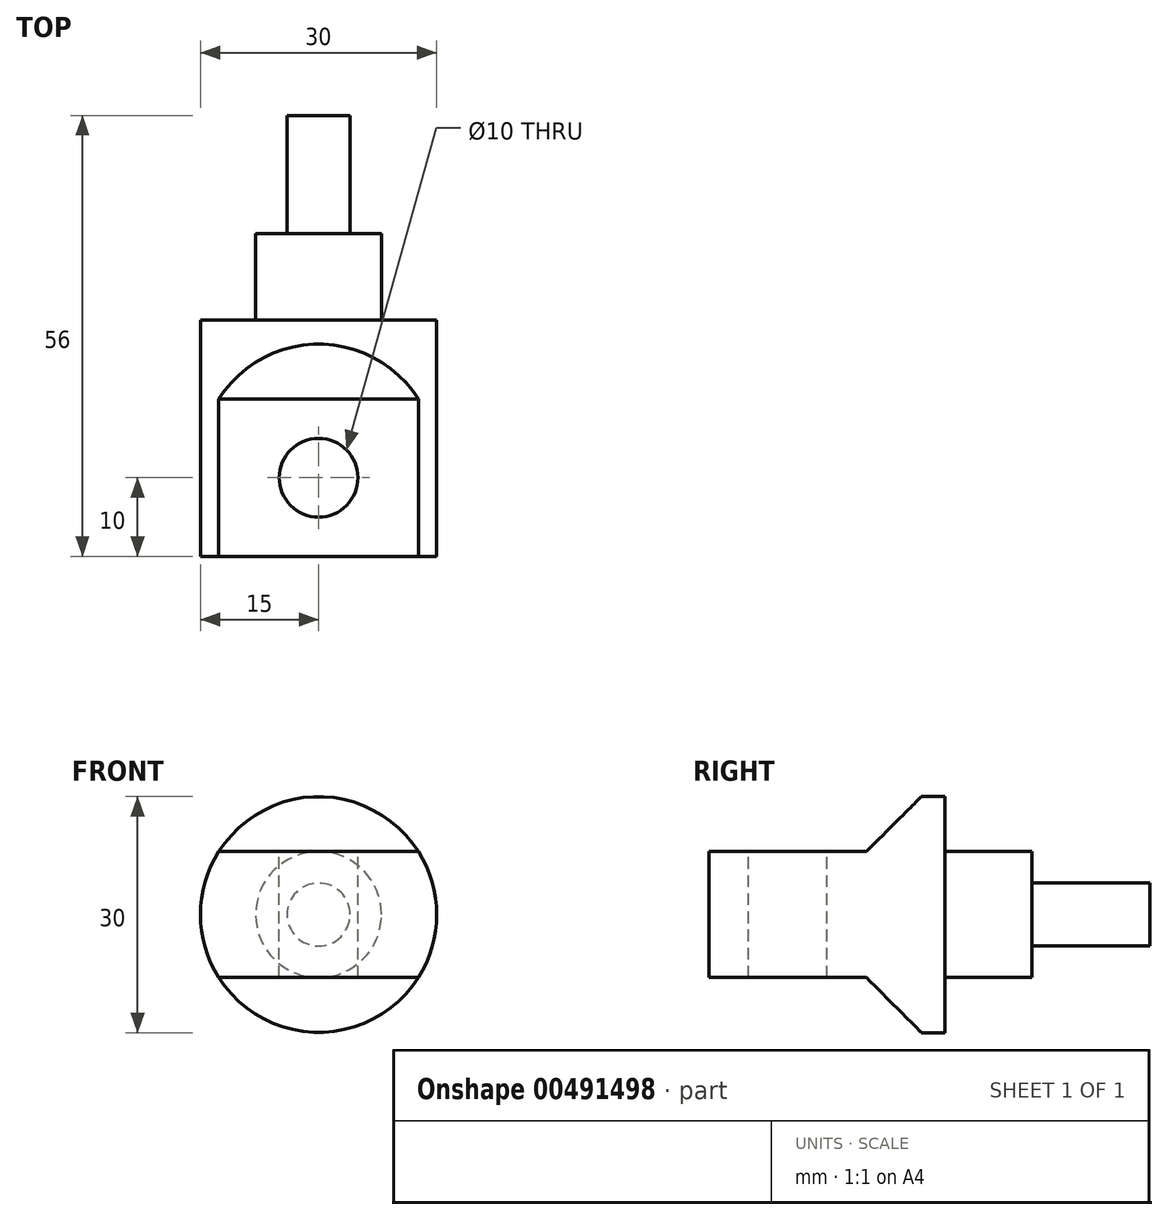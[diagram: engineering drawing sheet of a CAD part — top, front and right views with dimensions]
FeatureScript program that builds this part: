
annotation { "Feature Type Name" : "Feature", "Feature Type Description" : "" }
export const myFeature = defineFeature(function(context is Context, id is Id, definition is map)
    precondition{}
    {
        {
            var Q0;
            Q0=qCreatedBy(makeId("Front.planeOp"),FACE);
            var sketch = newSketch(context, id + "F0", { "sketchPlane" : qUnion([Q0])});
            skCircle(sketch, "E0", {"center": v(0, 0) * mm, "radius": 15 * mm});
            skSolve(sketch);
        }
        {
            var Q0;
            Q0=makeQuery(id+"F0.imprint","IMPRINT",FACE,{"disambiguationData":[TD([[makeQuery(id+"F0.imprint","IMPRINT",EDGE,{"derivedFrom":sQuery(id+"F0.wireOp",EDGE,"E0")}),1.0]])]});
            extrude(context, id + "F1", {"entities" : qUnion([Q0]), "depth" : 30 * mm});
        }
        {
            var Q0;
            Q0=qCreatedBy(makeId("Top.planeOp"),FACE);
            cPlane(context, id + "F2", {"entities" : qUnion([Q0]), "cplaneType" : CPlaneType.OFFSET, "offset" : 15 * mm, "width" : 150 * mm, "height" : 150 * mm});
        }
        {
            var Q0;
            Q0=qCreatedBy(id+"F2.planeOp",FACE);
            var sketch = newSketch(context, id + "F3", { "sketchPlane" : qUnion([Q0])});
            skLineSegment(sketch, "E1", {"start": v(15, 0) * mm, "end": v(15, -30) * mm});
            skLineSegment(sketch, "E2", {"start": v(-15, -30) * mm, "end": v(-15, 0) * mm});
            skLineSegment(sketch, "E3.bottom", {"start": v(-15, -30) * mm, "end": v(15, -30) * mm});
            skLineSegment(sketch, "E3.top", {"start": v(-15, -10) * mm, "end": v(15, -10) * mm});
            skLineSegment(sketch, "E3.left", {"start": v(-15, -30) * mm, "end": v(-15, -10) * mm});
            skLineSegment(sketch, "E3.right", {"start": v(15, -30) * mm, "end": v(15, -10) * mm});
            skSolve(sketch);
        }
        {
            var Q0;
            Q0=makeQuery(id+"F3.imprint","IMPRINT",FACE,{"disambiguationData":[TD([[makeQuery(id+"F3.imprint","IMPRINT",EDGE,{"derivedFrom":sQuery(id+"F3.wireOp",EDGE,"E3.bottom")}),1.0]])]});
            extrude(context, id + "F4", {"entities" : qUnion([Q0]), "operationType" : NewBodyOperationType.REMOVE, "oppositeDirection" : true, "depth" : 7 * mm});
        }
        {
            var Q0;
            Q0=qCreatedBy(makeId("Top.planeOp"),FACE);
            cPlane(context, id + "F5", {"entities" : qUnion([Q0]), "cplaneType" : CPlaneType.OFFSET, "offset" : 15 * mm, "oppositeDirection" : true, "width" : 150 * mm, "height" : 150 * mm});
        }
        {
            var Q0;
            Q0=qCreatedBy(id+"F5.planeOp",FACE);
            var sketch = newSketch(context, id + "F6", { "sketchPlane" : qUnion([Q0])});
            skLineSegment(sketch, "E4", {"start": v(15, 0) * mm, "end": v(15, -30) * mm});
            skLineSegment(sketch, "E5", {"start": v(-15, -30) * mm, "end": v(-15, 0) * mm});
            skLineSegment(sketch, "E6.bottom", {"start": v(15, -30) * mm, "end": v(-15, -30) * mm});
            skLineSegment(sketch, "E6.top", {"start": v(15, -10) * mm, "end": v(-15, -10) * mm});
            skLineSegment(sketch, "E6.left", {"start": v(15, -30) * mm, "end": v(15, -10) * mm});
            skLineSegment(sketch, "E6.right", {"start": v(-15, -30) * mm, "end": v(-15, -10) * mm});
            skSolve(sketch);
        }
        {
            var Q0;
            Q0=makeQuery(id+"F6.imprint","IMPRINT",FACE,{"disambiguationData":[TD([[makeQuery(id+"F6.imprint","IMPRINT",EDGE,{"derivedFrom":sQuery(id+"F6.wireOp",EDGE,"E6.bottom")}),-1.0]])]});
            extrude(context, id + "F7", {"entities" : qUnion([Q0]), "operationType" : NewBodyOperationType.REMOVE, "depth" : 7 * mm});
        }
        {
            var Q0;
            Q0=qCreatedBy(makeId("Right.planeOp"),FACE);
            cPlane(context, id + "F8", {"entities" : qUnion([Q0]), "cplaneType" : CPlaneType.OFFSET, "offset" : 15 * mm, "width" : 150 * mm, "height" : 150 * mm});
        }
        {
            var Q0;
            Q0=qCreatedBy(id+"F8.planeOp",FACE);
            var sketch = newSketch(context, id + "F9", { "sketchPlane" : qUnion([Q0])});
            skLineSegment(sketch, "E7", {"start": v(4, -15) * mm, "end": v(-10, -15) * mm});
            skLineSegment(sketch, "E8", {"start": v(-10, 15) * mm, "end": v(0, 15) * mm});
            skLineSegment(sketch, "E9", {"start": v(-10, 8) * mm, "end": v(-3, 15) * mm});
            skLineSegment(sketch, "E10", {"start": v(-10, 15) * mm, "end": v(-10, 8) * mm});
            skLineSegment(sketch, "E11", {"start": v(-10, 15) * mm, "end": v(-3, 15) * mm});
            skLineSegment(sketch, "E12", {"start": v(-10, -15) * mm, "end": v(-10, -8) * mm});
            skLineSegment(sketch, "E13", {"start": v(-10, -8) * mm, "end": v(-3, -15) * mm});
            skLineSegment(sketch, "E14", {"start": v(-3, -15) * mm, "end": v(-10, -15) * mm});
            skSolve(sketch);
        }
        {
            var Q0;
            Q0=makeQuery(id+"F9.imprint","IMPRINT",FACE,{"disambiguationData":[TD([[makeQuery(id+"F9.imprint","IMPRINT",EDGE,{"derivedFrom":sQuery(id+"F9.wireOp",EDGE,"E9")}),1.0]])]});
            var Q1;
            Q1=makeQuery(id+"F9.imprint","IMPRINT",FACE,{"disambiguationData":[TD([[makeQuery(id+"F9.imprint","IMPRINT",EDGE,{"derivedFrom":sQuery(id+"F9.wireOp",EDGE,"E12")}),-1.0]])]});
            extrude(context, id + "F10", {"entities" : qUnion([Q0, Q1]), "operationType" : NewBodyOperationType.REMOVE, "oppositeDirection" : true, "depth" : 30 * mm});
        }
        {
            var Q0;
            Q0=makeQuery(id+"F1.opExtrude","CAP_FACE",FACE,{"disambiguationData":[OSD([sQuery(id+"F0.wireOp",EDGE,"E0")])],"isStart":true});
            var sketch = newSketch(context, id + "F11", { "sketchPlane" : qUnion([Q0])});
            skCircle(sketch, "E15", {"center": v(0, 0) * mm, "radius": 8 * mm});
            skSolve(sketch);
        }
        {
            var Q0;
            Q0=makeQuery(id+"F11.imprint","IMPRINT",FACE,{"disambiguationData":[TD([[makeQuery(id+"F11.imprint","IMPRINT",EDGE,{"derivedFrom":sQuery(id+"F11.wireOp",EDGE,"E15")}),1.0]])]});
            extrude(context, id + "F12", {"entities" : qUnion([Q0]), "operationType" : NewBodyOperationType.ADD, "depth" : 11 * mm});
        }
        {
            var Q0;
            Q0=makeQuery(id+"F12.opExtrude","CAP_FACE",FACE,{"disambiguationData":[OSD([sQuery(id+"F11.wireOp",EDGE,"E15")])],"isStart":false});
            var sketch = newSketch(context, id + "F13", { "sketchPlane" : qUnion([Q0])});
            skCircle(sketch, "E16", {"center": v(0, 0) * mm, "radius": 4 * mm});
            skSolve(sketch);
        }
        {
            var Q0;
            Q0=makeQuery(id+"F13.imprint","IMPRINT",FACE,{"disambiguationData":[TD([[makeQuery(id+"F13.imprint","IMPRINT",EDGE,{"derivedFrom":sQuery(id+"F13.wireOp",EDGE,"E16")}),1.0]])]});
            extrude(context, id + "F14", {"entities" : qUnion([Q0]), "operationType" : NewBodyOperationType.ADD, "depth" : 15 * mm});
        }
        {
            var Q0;
            Q0=makeQuery(id+"F4.boolean.opBoolean","COPY",FACE,{"derivedFrom":makeQuery(id+"F4.opExtrude","CAP_FACE",FACE,{"disambiguationData":[OSD([sQuery(id+"F3.wireOp",EDGE,"E3.bottom"),sQuery(id+"F3.wireOp",EDGE,"E3.top"),sQuery(id+"F3.wireOp",EDGE,"E3.left"),sQuery(id+"F3.wireOp",EDGE,"E3.right")])],"isStart":false})});
            var sketch = newSketch(context, id + "F15", { "sketchPlane" : qUnion([Q0])});
            skCircle(sketch, "E17", {"center": v(0, -20) * mm, "radius": 5 * mm});
            skPoint(sketch, "E17.centerSnap0", {"position": v(0, -10) * mm});
            skLineSegment(sketch, "E18", {"start": v(15, 0) * mm, "end": v(15, -30) * mm});
            skSolve(sketch);
        }
        {
            var Q0;
            Q0=makeQuery(id+"F15.imprint","IMPRINT",FACE,{"disambiguationData":[TD([[makeQuery(id+"F15.imprint","IMPRINT",EDGE,{"derivedFrom":sQuery(id+"F15.wireOp",EDGE,"E17")}),1.0]])]});
            extrude(context, id + "F16", {"entities" : qUnion([Q0]), "operationType" : NewBodyOperationType.REMOVE, "endBound" : BoundingType.THROUGH_ALL, "oppositeDirection" : true, "depth" : 25 * mm});
        }
    });
